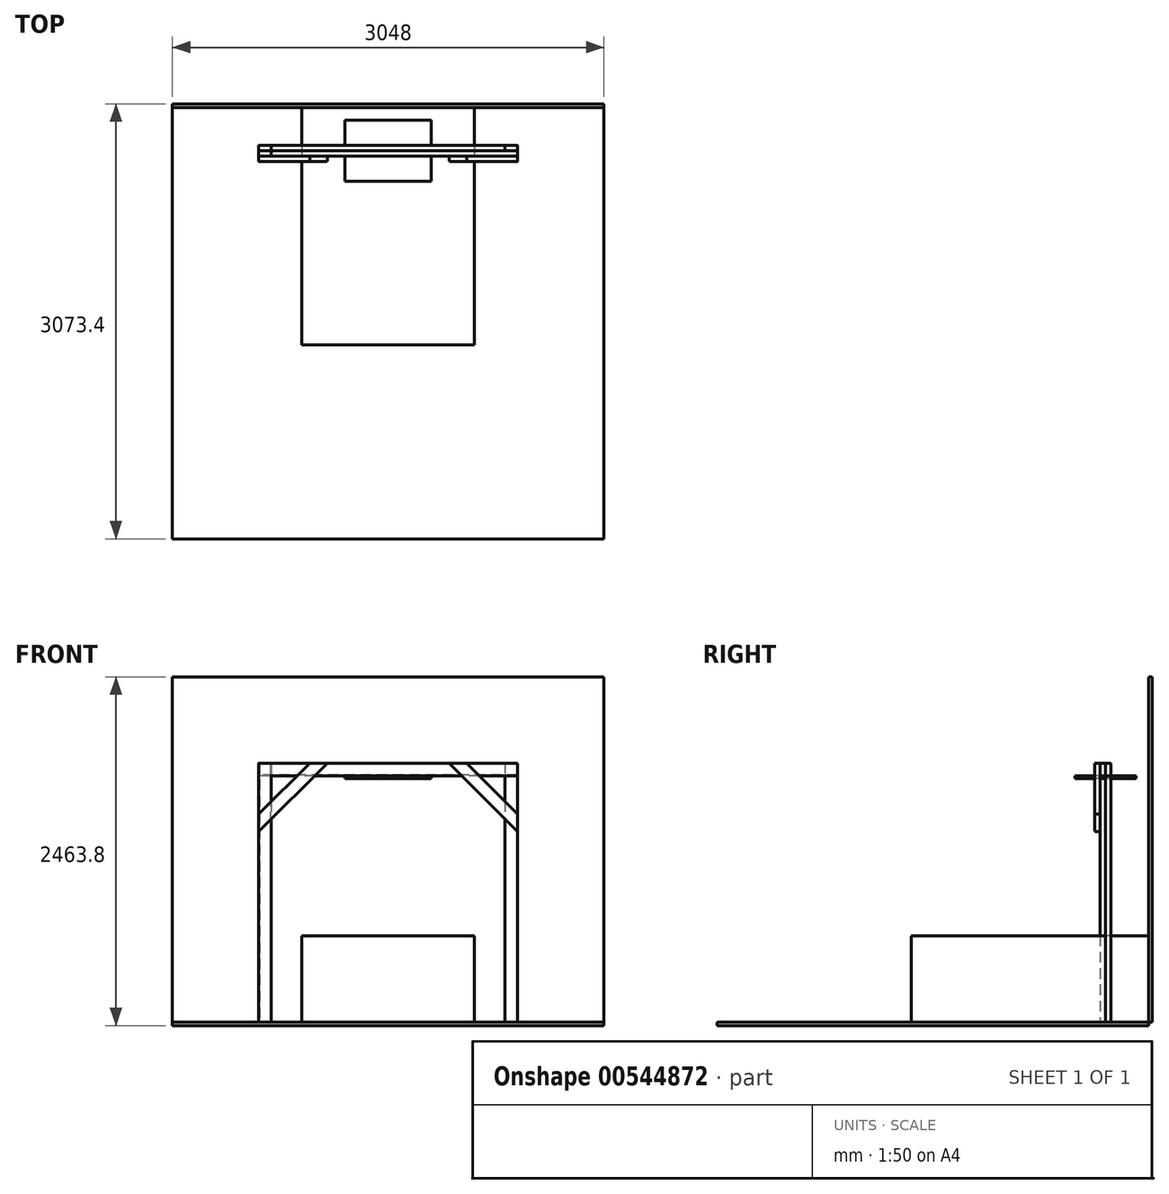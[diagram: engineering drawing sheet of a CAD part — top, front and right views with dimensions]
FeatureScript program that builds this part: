
annotation { "Feature Type Name" : "Feature", "Feature Type Description" : "" }
export const myFeature = defineFeature(function(context is Context, id is Id, definition is map)
    precondition{}
    {
        {
            var Q0;
            Q0=qCreatedBy(makeId("Top.planeOp"),FACE);
            var sketch = newSketch(context, id + "F0", { "sketchPlane" : qUnion([Q0])});
            skLineSegment(sketch, "E0.bottom", {"start": v(-1524, -3048) * mm, "end": v(1524, -3048) * mm});
            skLineSegment(sketch, "E0.top", {"start": v(-1524, 0) * mm, "end": v(1524, 0) * mm});
            skLineSegment(sketch, "E0.left", {"start": v(-1524, -3048) * mm, "end": v(-1524, 0) * mm});
            skLineSegment(sketch, "E0.right", {"start": v(1524, -3048) * mm, "end": v(1524, 0) * mm});
            skSolve(sketch);
        }
        {
            var Q0;
            Q0=qCreatedBy(makeId("Front.planeOp"),FACE);
            var sketch = newSketch(context, id + "F1", { "sketchPlane" : qUnion([Q0])});
            skLineSegment(sketch, "E1.bottom", {"start": v(-1524, 2438.4) * mm, "end": v(1524, 2438.4) * mm});
            skLineSegment(sketch, "E1.top", {"start": v(-1524, 0) * mm, "end": v(1524, 0) * mm});
            skLineSegment(sketch, "E1.left", {"start": v(-1524, 2438.4) * mm, "end": v(-1524, 0) * mm});
            skLineSegment(sketch, "E1.right", {"start": v(1524, 2438.4) * mm, "end": v(1524, 0) * mm});
            skSolve(sketch);
        }
        {
            var Q0;
            Q0=makeQuery(id+"F1.imprint","IMPRINT",FACE,{"disambiguationData":[TD([[makeQuery(id+"F1.imprint","IMPRINT",EDGE,{"derivedFrom":sQuery(id+"F1.wireOp",EDGE,"E1.bottom")}),-1.0]])]});
            extrude(context, id + "F2", {"entities" : qUnion([Q0]), "oppositeDirection" : true, "depth" : 25.4 * mm, "offsetDistance" : 25.4 * mm});
        }
        {
            var Q0;
            Q0=makeQuery(id+"F0.imprint","IMPRINT",FACE,{"disambiguationData":[TD([[makeQuery(id+"F0.imprint","IMPRINT",EDGE,{"derivedFrom":sQuery(id+"F0.wireOp",EDGE,"E0.bottom")}),1.0]])]});
            extrude(context, id + "F3", {"entities" : qUnion([Q0]), "oppositeDirection" : true, "depth" : 25.4 * mm, "offsetDistance" : 25.4 * mm});
        }
        {
            var Q0;
            Q0=qCreatedBy(makeId("Top.planeOp"),FACE);
            var sketch = newSketch(context, id + "F4", { "sketchPlane" : qUnion([Q0])});
            skLineSegment(sketch, "E2.bottom", {"start": v(-609.6, 0) * mm, "end": v(609.6, 0) * mm});
            skLineSegment(sketch, "E2.top", {"start": v(-609.6, -1676.4) * mm, "end": v(609.6, -1676.4) * mm});
            skLineSegment(sketch, "E2.left", {"start": v(-609.6, 0) * mm, "end": v(-609.6, -1676.4) * mm});
            skLineSegment(sketch, "E2.right", {"start": v(609.6, 0) * mm, "end": v(609.6, -1676.4) * mm});
            skSolve(sketch);
        }
        {
            var Q0;
            Q0=makeQuery(id+"F4.imprint","IMPRINT",FACE,{"disambiguationData":[TD([[makeQuery(id+"F4.imprint","IMPRINT",EDGE,{"derivedFrom":sQuery(id+"F4.wireOp",EDGE,"E2.bottom")}),-1.0]])]});
            extrude(context, id + "F5", {"entities" : qUnion([Q0]), "depth" : 609.6 * mm, "offsetDistance" : 25.4 * mm});
        }
        {
            var Q0;
            Q0=qCreatedBy(makeId("Top.planeOp"),FACE);
            var sketch = newSketch(context, id + "F6", { "sketchPlane" : qUnion([Q0])});
            skLineSegment(sketch, "E3.bottom", {"start": v(-831.85, -304.8) * mm, "end": v(-908.05, -304.8) * mm});
            skLineSegment(sketch, "E3.top", {"start": v(-831.85, -342.9) * mm, "end": v(-908.05, -342.9) * mm});
            skLineSegment(sketch, "E3.left", {"start": v(-825.5, -311.15) * mm, "end": v(-825.5, -336.55) * mm});
            skLineSegment(sketch, "E3.right", {"start": v(-914.4, -311.15) * mm, "end": v(-914.4, -336.55) * mm});
            skPoint(sketch, "E3.middle", {"position": v(-869.95, -323.85) * mm});
            skPoint(sketch, "E4.visualSharp", {"position": v(-914.4, -304.8) * mm});
            skArc(sketch, "E4.filletArc", {"start": v(-908.05, -304.8) * mm, "mid": v(-912.54, -306.66) * mm, "end": v(-914.4, -311.15) * mm});
            skPoint(sketch, "E5.visualSharp", {"position": v(-914.4, -342.9) * mm});
            skArc(sketch, "E5.filletArc", {"start": v(-914.4, -336.55) * mm, "mid": v(-912.54, -341.04) * mm, "end": v(-908.05, -342.9) * mm});
            skPoint(sketch, "E6.visualSharp", {"position": v(-825.5, -304.8) * mm});
            skArc(sketch, "E6.filletArc", {"start": v(-825.5, -311.15) * mm, "mid": v(-827.36, -306.66) * mm, "end": v(-831.85, -304.8) * mm});
            skPoint(sketch, "E7.visualSharp", {"position": v(-825.5, -342.9) * mm});
            skArc(sketch, "E7.filletArc", {"start": v(-831.85, -342.9) * mm, "mid": v(-827.36, -341.04) * mm, "end": v(-825.5, -336.55) * mm});
            skPoint(sketch, "E8.MirrorP", {"position": v(-914.4, -266.7) * mm});
            skLineSegment(sketch, "E9.MirrorCS", {"start": v(-831.85, -266.7) * mm, "end": v(-908.05, -266.7) * mm});
            skLineSegment(sketch, "E10.MirrorCS", {"start": v(-825.5, -298.45) * mm, "end": v(-825.5, -273.05) * mm});
            skPoint(sketch, "E11.MirrorP", {"position": v(-825.5, -266.7) * mm});
            skLineSegment(sketch, "E12.MirrorCS", {"start": v(-914.4, -298.45) * mm, "end": v(-914.4, -273.05) * mm});
            skArc(sketch, "E13.MirrorCS", {"start": v(-908.05, -304.8) * mm, "mid": v(-912.54, -302.94) * mm, "end": v(-914.4, -298.45) * mm});
            skArc(sketch, "E14.MirrorCS", {"start": v(-914.4, -273.05) * mm, "mid": v(-912.54, -268.56) * mm, "end": v(-908.05, -266.7) * mm});
            skArc(sketch, "E15.MirrorCS", {"start": v(-825.5, -298.45) * mm, "mid": v(-827.36, -302.94) * mm, "end": v(-831.85, -304.8) * mm});
            skArc(sketch, "E16.MirrorCS", {"start": v(-831.85, -266.7) * mm, "mid": v(-827.36, -268.56) * mm, "end": v(-825.5, -273.05) * mm});
            skPoint(sketch, "E17.MirrorP", {"position": v(-869.95, -285.75) * mm});
            skLineSegment(sketch, "E18", {"start": v(0, 0) * mm, "end": v(0, -569.7) * mm, "construction": true});
            skArc(sketch, "E19.MirrorCS", {"start": v(908.05, -304.8) * mm, "mid": v(912.54, -302.94) * mm, "end": v(914.4, -298.45) * mm});
            skArc(sketch, "E20.MirrorCS", {"start": v(908.05, -304.8) * mm, "mid": v(912.54, -306.66) * mm, "end": v(914.4, -311.15) * mm});
            skArc(sketch, "E21.MirrorCS", {"start": v(825.5, -311.15) * mm, "mid": v(827.36, -306.66) * mm, "end": v(831.85, -304.8) * mm});
            skArc(sketch, "E22.MirrorCS", {"start": v(914.4, -336.55) * mm, "mid": v(912.54, -341.04) * mm, "end": v(908.05, -342.9) * mm});
            skLineSegment(sketch, "E23.MirrorCS", {"start": v(914.4, -311.15) * mm, "end": v(914.4, -336.55) * mm});
            skArc(sketch, "E24.MirrorCS", {"start": v(825.5, -298.45) * mm, "mid": v(827.36, -302.94) * mm, "end": v(831.85, -304.8) * mm});
            skArc(sketch, "E25.MirrorCS", {"start": v(914.4, -273.05) * mm, "mid": v(912.54, -268.56) * mm, "end": v(908.05, -266.7) * mm});
            skLineSegment(sketch, "E26.MirrorCS", {"start": v(914.4, -298.45) * mm, "end": v(914.4, -273.05) * mm});
            skLineSegment(sketch, "E27.MirrorCS", {"start": v(825.5, -298.45) * mm, "end": v(825.5, -273.05) * mm});
            skArc(sketch, "E28.MirrorCS", {"start": v(831.85, -342.9) * mm, "mid": v(827.36, -341.04) * mm, "end": v(825.5, -336.55) * mm});
            skLineSegment(sketch, "E29.MirrorCS", {"start": v(825.5, -311.15) * mm, "end": v(825.5, -336.55) * mm});
            skArc(sketch, "E30.MirrorCS", {"start": v(831.85, -266.7) * mm, "mid": v(827.36, -268.56) * mm, "end": v(825.5, -273.05) * mm});
            skLineSegment(sketch, "E31.MirrorCS", {"start": v(831.85, -304.8) * mm, "end": v(908.05, -304.8) * mm});
            skPoint(sketch, "E32.MirrorP", {"position": v(825.5, -304.8) * mm});
            skPoint(sketch, "E33.MirrorP", {"position": v(914.4, -304.8) * mm});
            skPoint(sketch, "E34.MirrorP", {"position": v(914.4, -266.7) * mm});
            skPoint(sketch, "E35.MirrorP", {"position": v(869.95, -285.75) * mm});
            skLineSegment(sketch, "E36.MirrorCS", {"start": v(831.85, -342.9) * mm, "end": v(908.05, -342.9) * mm});
            skLineSegment(sketch, "E37.MirrorCS", {"start": v(831.85, -266.7) * mm, "end": v(908.05, -266.7) * mm});
            skPoint(sketch, "E38.MirrorP", {"position": v(914.4, -342.9) * mm});
            skPoint(sketch, "E39.MirrorP", {"position": v(825.5, -266.7) * mm});
            skPoint(sketch, "E40.MirrorP", {"position": v(869.95, -323.85) * mm});
            skPoint(sketch, "E41.MirrorP", {"position": v(825.5, -342.9) * mm});
            skSolve(sketch);
        }
        {
            var Q0;
            Q0=makeQuery(id+"F6.imprint","IMPRINT",FACE,{"disambiguationData":[TD([[makeQuery(id+"F6.imprint","IMPRINT",EDGE,{"derivedFrom":sQuery(id+"F6.wireOp",EDGE,"E3.bottom")}),-1.0]])]});
            var Q1;
            Q1=makeQuery(id+"F6.imprint","IMPRINT",FACE,{"disambiguationData":[TD([[makeQuery(id+"F6.imprint","IMPRINT",EDGE,{"derivedFrom":sQuery(id+"F6.wireOp",EDGE,"E3.bottom")}),1.0]])]});
            var Q2;
            Q2=makeQuery(id+"F6.imprint","IMPRINT",FACE,{"disambiguationData":[TD([[makeQuery(id+"F6.imprint","IMPRINT",EDGE,{"derivedFrom":sQuery(id+"F6.wireOp",EDGE,"E19.MirrorCS")}),1.0]])]});
            var Q3;
            Q3=makeQuery(id+"F6.imprint","IMPRINT",FACE,{"disambiguationData":[TD([[makeQuery(id+"F6.imprint","IMPRINT",EDGE,{"derivedFrom":sQuery(id+"F6.wireOp",EDGE,"E20.MirrorCS")}),-1.0]])]});
            extrude(context, id + "F7", {"entities" : qUnion([Q0, Q1, Q2, Q3]), "depth" : 1828.8 * mm, "offsetDistance" : 25.4 * mm});
        }
        {
            var Q0;
            Q0=qCreatedBy(makeId("Right.planeOp"),FACE);
            var sketch = newSketch(context, id + "F8", { "sketchPlane" : qUnion([Q0])});
            skLineSegment(sketch, "E42.bottom", {"start": v(-266.7, 1746.25) * mm, "end": v(-266.7, 1822.45) * mm});
            skLineSegment(sketch, "E42.top", {"start": v(-304.8, 1746.25) * mm, "end": v(-304.8, 1822.45) * mm});
            skLineSegment(sketch, "E42.left", {"start": v(-273.05, 1739.9) * mm, "end": v(-298.45, 1739.9) * mm});
            skLineSegment(sketch, "E42.right", {"start": v(-273.05, 1828.8) * mm, "end": v(-298.45, 1828.8) * mm});
            skPoint(sketch, "E42.middle", {"position": v(-285.75, 1784.35) * mm});
            skPoint(sketch, "E43.visualSharp", {"position": v(-266.7, 1828.8) * mm});
            skArc(sketch, "E43.filletArc", {"start": v(-266.7, 1822.45) * mm, "mid": v(-268.56, 1826.94) * mm, "end": v(-273.05, 1828.8) * mm});
            skPoint(sketch, "E44.visualSharp", {"position": v(-304.8, 1828.8) * mm});
            skArc(sketch, "E44.filletArc", {"start": v(-298.45, 1828.8) * mm, "mid": v(-302.94, 1826.94) * mm, "end": v(-304.8, 1822.45) * mm});
            skPoint(sketch, "E45.visualSharp", {"position": v(-266.7, 1739.9) * mm});
            skArc(sketch, "E45.filletArc", {"start": v(-273.05, 1739.9) * mm, "mid": v(-268.56, 1741.76) * mm, "end": v(-266.7, 1746.25) * mm});
            skPoint(sketch, "E46.visualSharp", {"position": v(-304.8, 1739.9) * mm});
            skArc(sketch, "E46.filletArc", {"start": v(-304.8, 1746.25) * mm, "mid": v(-302.94, 1741.76) * mm, "end": v(-298.45, 1739.9) * mm});
            skArc(sketch, "E47.MirrorCS", {"start": v(-342.9, 1822.45) * mm, "mid": v(-341.04, 1826.94) * mm, "end": v(-336.55, 1828.8) * mm});
            skArc(sketch, "E48.MirrorCS", {"start": v(-311.15, 1828.8) * mm, "mid": v(-306.66, 1826.94) * mm, "end": v(-304.8, 1822.45) * mm});
            skArc(sketch, "E49.MirrorCS", {"start": v(-336.55, 1739.9) * mm, "mid": v(-341.04, 1741.76) * mm, "end": v(-342.9, 1746.25) * mm});
            skArc(sketch, "E50.MirrorCS", {"start": v(-304.8, 1746.25) * mm, "mid": v(-306.66, 1741.76) * mm, "end": v(-311.15, 1739.9) * mm});
            skLineSegment(sketch, "E51.MirrorCS", {"start": v(-336.55, 1828.8) * mm, "end": v(-311.15, 1828.8) * mm});
            skLineSegment(sketch, "E52.MirrorCS", {"start": v(-342.9, 1746.25) * mm, "end": v(-342.9, 1822.45) * mm});
            skLineSegment(sketch, "E53.MirrorCS", {"start": v(-336.55, 1739.9) * mm, "end": v(-311.15, 1739.9) * mm});
            skPoint(sketch, "E54.MirrorP", {"position": v(-342.9, 1828.8) * mm});
            skPoint(sketch, "E55.MirrorP", {"position": v(-323.85, 1784.35) * mm});
            skPoint(sketch, "E56.MirrorP", {"position": v(-342.9, 1739.9) * mm});
            skSolve(sketch);
        }
        {
            var Q0;
            Q0=makeQuery(id+"F8.imprint","IMPRINT",FACE,{"disambiguationData":[TD([[makeQuery(id+"F8.imprint","IMPRINT",EDGE,{"derivedFrom":sQuery(id+"F8.wireOp",EDGE,"E42.bottom")}),1.0]])]});
            var Q1;
            Q1=makeQuery(id+"F8.imprint","IMPRINT",FACE,{"disambiguationData":[TD([[makeQuery(id+"F8.imprint","IMPRINT",EDGE,{"derivedFrom":sQuery(id+"F8.wireOp",EDGE,"E42.top")}),1.0]])]});
            var Q2;
            Q2=makeQuery(id+"F7.opExtrude","SWEPT_FACE",FACE,{"disambiguationData":[OSD([sQuery(id+"F6.wireOp",EDGE,"E26.MirrorCS")])]});
            var Q3;
            Q3=makeQuery(id+"F7.opExtrude","SWEPT_FACE",FACE,{"disambiguationData":[OSD([sQuery(id+"F6.wireOp",EDGE,"E12.MirrorCS")])]});
            extrude(context, id + "F9", {"entities" : qUnion([Q0, Q1]), "endBound" : BoundingType.UP_TO_SURFACE, "depth" : 25.4 * mm, "endBoundEntityFace" : qUnion([Q2]), "offsetDistance" : 25.4 * mm, "hasSecondDirection" : true, "secondDirectionBound" : SecondDirectionBoundingType.UP_TO_SURFACE, "secondDirectionOppositeDirection" : true, "secondDirectionDepth" : 25.4 * mm, "secondDirectionBoundEntityFace" : qUnion([Q3])});
        }
        {
            var Q0;
            Q0=makeQuery(id+"F9.opExtrude","SWEPT_FACE",FACE,{"disambiguationData":[OSD([sQuery(id+"F8.wireOp",EDGE,"E42.left")])]});
            var sketch = newSketch(context, id + "F10", { "sketchPlane" : qUnion([Q0])});
            skLineSegment(sketch, "E57.bottom", {"start": v(304.8, 88.9) * mm, "end": v(-304.8, 88.9) * mm});
            skLineSegment(sketch, "E57.top", {"start": v(304.8, 520.7) * mm, "end": v(-304.8, 520.7) * mm});
            skLineSegment(sketch, "E57.left", {"start": v(304.8, 88.9) * mm, "end": v(304.8, 520.7) * mm});
            skLineSegment(sketch, "E57.right", {"start": v(-304.8, 88.9) * mm, "end": v(-304.8, 520.7) * mm});
            skPoint(sketch, "E57.middle", {"position": v(0, 304.8) * mm});
            skSolve(sketch);
        }
        {
            var Q0;
            Q0 = qSketchRegion(id + "F10", true);
            extrude(context, id + "F11", {"entities" : qUnion([Q0]), "depth" : 19.05 * mm, "offsetDistance" : 25.4 * mm});
        }
        {
            var Q0;
            Q0=makeQuery(id+"F7.opExtrude","CAP_EDGE",EDGE,{"disambiguationData":[OSD([sQuery(id+"F6.wireOp",EDGE,"E3.right")])],"isStart":false});
            cPlane(context, id + "F12", {"entities" : qUnion([Q0]), "cplaneType" : CPlaneType.LINE_ANGLE, "offset" : 25.4 * mm, "angle" : 135 * degree, "width" : 152.4 * mm, "height" : 152.4 * mm});
        }
        {
            var Q0;
            Q0=qCreatedBy(id+"F12.planeOp",FACE);
            var sketch = newSketch(context, id + "F13", { "sketchPlane" : qUnion([Q0])});
            skLineSegment(sketch, "E58.bottom", {"start": v(-342.9, 1603.19) * mm, "end": v(-342.9, 1679.39) * mm});
            skLineSegment(sketch, "E58.top", {"start": v(-381, 1603.19) * mm, "end": v(-381, 1679.39) * mm});
            skLineSegment(sketch, "E58.left", {"start": v(-349.25, 1596.84) * mm, "end": v(-374.65, 1596.84) * mm});
            skLineSegment(sketch, "E58.right", {"start": v(-349.25, 1685.74) * mm, "end": v(-374.65, 1685.74) * mm});
            skPoint(sketch, "E58.middle", {"position": v(-361.95, 1641.29) * mm});
            skPoint(sketch, "E59.visualSharp", {"position": v(-342.9, 1685.74) * mm});
            skArc(sketch, "E59.filletArc", {"start": v(-342.9, 1679.39) * mm, "mid": v(-344.76, 1683.88) * mm, "end": v(-349.25, 1685.74) * mm});
            skPoint(sketch, "E60.visualSharp", {"position": v(-381, 1685.74) * mm});
            skArc(sketch, "E60.filletArc", {"start": v(-374.65, 1685.74) * mm, "mid": v(-379.14, 1683.88) * mm, "end": v(-381, 1679.39) * mm});
            skPoint(sketch, "E61.visualSharp", {"position": v(-342.9, 1596.84) * mm});
            skArc(sketch, "E61.filletArc", {"start": v(-349.25, 1596.84) * mm, "mid": v(-344.76, 1598.7) * mm, "end": v(-342.9, 1603.19) * mm});
            skPoint(sketch, "E62.visualSharp", {"position": v(-381, 1596.84) * mm});
            skArc(sketch, "E62.filletArc", {"start": v(-381, 1603.19) * mm, "mid": v(-379.14, 1598.7) * mm, "end": v(-374.65, 1596.84) * mm});
            skLineSegment(sketch, "E63", {"start": v(-342.9, 1898.45) * mm, "end": v(-342.9, 1685.74) * mm, "construction": true});
            skLineSegment(sketch, "E64", {"start": v(-304.8, 1748.33) * mm, "end": v(-304.8, 1895.93) * mm, "construction": true});
            skArc(sketch, "E65.MirrorCS", {"start": v(-266.7, 1679.39) * mm, "mid": v(-264.84, 1683.88) * mm, "end": v(-260.35, 1685.74) * mm});
            skArc(sketch, "E66.MirrorCS", {"start": v(-228.6, 1603.19) * mm, "mid": v(-230.46, 1598.7) * mm, "end": v(-234.95, 1596.84) * mm});
            skArc(sketch, "E67.MirrorCS", {"start": v(-260.35, 1596.84) * mm, "mid": v(-264.84, 1598.7) * mm, "end": v(-266.7, 1603.19) * mm});
            skArc(sketch, "E68.MirrorCS", {"start": v(-234.95, 1685.74) * mm, "mid": v(-230.46, 1683.88) * mm, "end": v(-228.6, 1679.39) * mm});
            skLineSegment(sketch, "E69.MirrorCS", {"start": v(-260.35, 1685.74) * mm, "end": v(-234.95, 1685.74) * mm});
            skLineSegment(sketch, "E70.MirrorCS", {"start": v(-260.35, 1596.84) * mm, "end": v(-234.95, 1596.84) * mm});
            skLineSegment(sketch, "E71.MirrorCS", {"start": v(-228.6, 1603.19) * mm, "end": v(-228.6, 1679.39) * mm});
            skLineSegment(sketch, "E72.MirrorCS", {"start": v(-266.7, 1603.19) * mm, "end": v(-266.7, 1679.39) * mm});
            skPoint(sketch, "E73.MirrorP", {"position": v(-247.65, 1641.29) * mm});
            skPoint(sketch, "E74.MirrorP", {"position": v(-266.7, 1685.74) * mm});
            skPoint(sketch, "E75.MirrorP", {"position": v(-228.6, 1685.74) * mm});
            skPoint(sketch, "E76.MirrorP", {"position": v(-266.7, 1596.84) * mm});
            skPoint(sketch, "E77.MirrorP", {"position": v(-228.6, 1596.84) * mm});
            skSolve(sketch);
        }
        {
            var Q0;
            Q0=makeQuery(id+"F13.imprint","IMPRINT",FACE,{"disambiguationData":[TD([[makeQuery(id+"F13.imprint","IMPRINT",EDGE,{"derivedFrom":sQuery(id+"F13.wireOp",EDGE,"E58.bottom")}),1.0]])]});
            var Q1;
            Q1=makeQuery(id+"F13.imprint","IMPRINT",FACE,{"disambiguationData":[TD([[makeQuery(id+"F13.imprint","IMPRINT",EDGE,{"derivedFrom":sQuery(id+"F13.wireOp",EDGE,"E65.MirrorCS")}),-1.0]])]});
            var Q2;
            Q2=makeQuery(id+"F9.opExtrude","SWEPT_FACE",FACE,{"disambiguationData":[OSD([sQuery(id+"F8.wireOp",EDGE,"E51.MirrorCS")])]});
            var Q3;
            Q3=makeQuery(id+"F7.opExtrude","SWEPT_FACE",FACE,{"disambiguationData":[OSD([sQuery(id+"F6.wireOp",EDGE,"E3.right")])]});
            extrude(context, id + "F14", {"entities" : qUnion([Q0, Q1]), "endBound" : BoundingType.UP_TO_SURFACE, "depth" : 25.4 * mm, "endBoundEntityFace" : qUnion([Q2]), "offsetDistance" : 25.4 * mm, "hasSecondDirection" : true, "secondDirectionBound" : SecondDirectionBoundingType.UP_TO_SURFACE, "secondDirectionOppositeDirection" : true, "secondDirectionDepth" : 25.4 * mm, "secondDirectionBoundEntityFace" : qUnion([Q3])});
        }
        {
            var Q0;
            Q0=makeQuery(id+"F14.opExtrude","SWEPT_BODY",BODY,{"disambiguationData":[OSD([sQuery(id+"F13.wireOp",EDGE,"E58.bottom"),sQuery(id+"F13.wireOp",EDGE,"E58.top"),sQuery(id+"F13.wireOp",EDGE,"E58.left"),sQuery(id+"F13.wireOp",EDGE,"E58.right"),sQuery(id+"F13.wireOp",EDGE,"E59.filletArc"),sQuery(id+"F13.wireOp",EDGE,"E60.filletArc"),sQuery(id+"F13.wireOp",EDGE,"E61.filletArc"),sQuery(id+"F13.wireOp",EDGE,"E62.filletArc")])]});
            var Q1;
            Q1=makeQuery(id+"F14.opExtrude","SWEPT_BODY",BODY,{"disambiguationData":[OSD([sQuery(id+"F13.wireOp",EDGE,"E65.MirrorCS"),sQuery(id+"F13.wireOp",EDGE,"E66.MirrorCS"),sQuery(id+"F13.wireOp",EDGE,"E67.MirrorCS"),sQuery(id+"F13.wireOp",EDGE,"E68.MirrorCS"),sQuery(id+"F13.wireOp",EDGE,"E69.MirrorCS"),sQuery(id+"F13.wireOp",EDGE,"E70.MirrorCS"),sQuery(id+"F13.wireOp",EDGE,"E71.MirrorCS"),sQuery(id+"F13.wireOp",EDGE,"E72.MirrorCS")])]});
            var Q2;
            Q2=qCreatedBy(makeId("Right.planeOp"),FACE);
            mirror(context, id + "F15", {"entities" : qUnion([Q0, Q1]), "mirrorPlane" : qUnion([Q2])});
        }
    });
